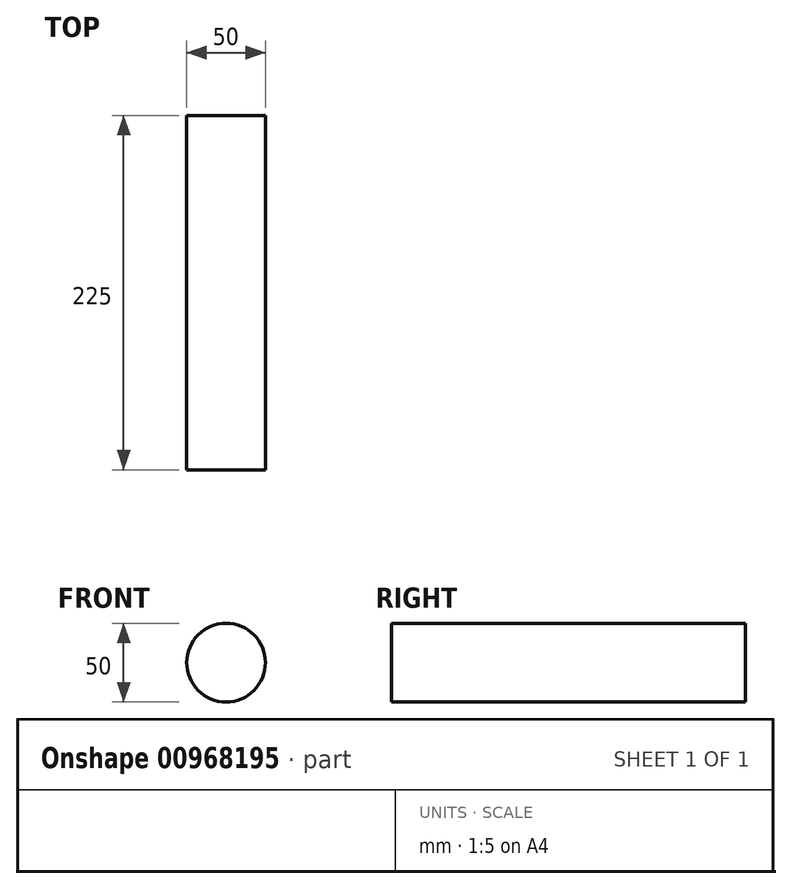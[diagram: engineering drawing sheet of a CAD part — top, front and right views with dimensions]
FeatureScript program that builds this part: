
annotation { "Feature Type Name" : "Feature", "Feature Type Description" : "" }
export const myFeature = defineFeature(function(context is Context, id is Id, definition is map)
    precondition{}
    {
        {
            var Q0;
            Q0=qCreatedBy(makeId("Front.planeOp"),FACE);
            var sketch = newSketch(context, id + "F0", { "sketchPlane" : qUnion([Q0])});
            skCircle(sketch, "E0", {"center": v(0, 0) * mm, "radius": 25 * mm});
            skSolve(sketch);
        }
        {
            var Q0;
            Q0 = qSketchRegion(id + "F0", true);
            extrude(context, id + "F1", {"entities" : qUnion([Q0]), "oppositeDirection" : true, "depth" : 225 * mm, "offsetDistance" : 25 * mm});
        }
    });
